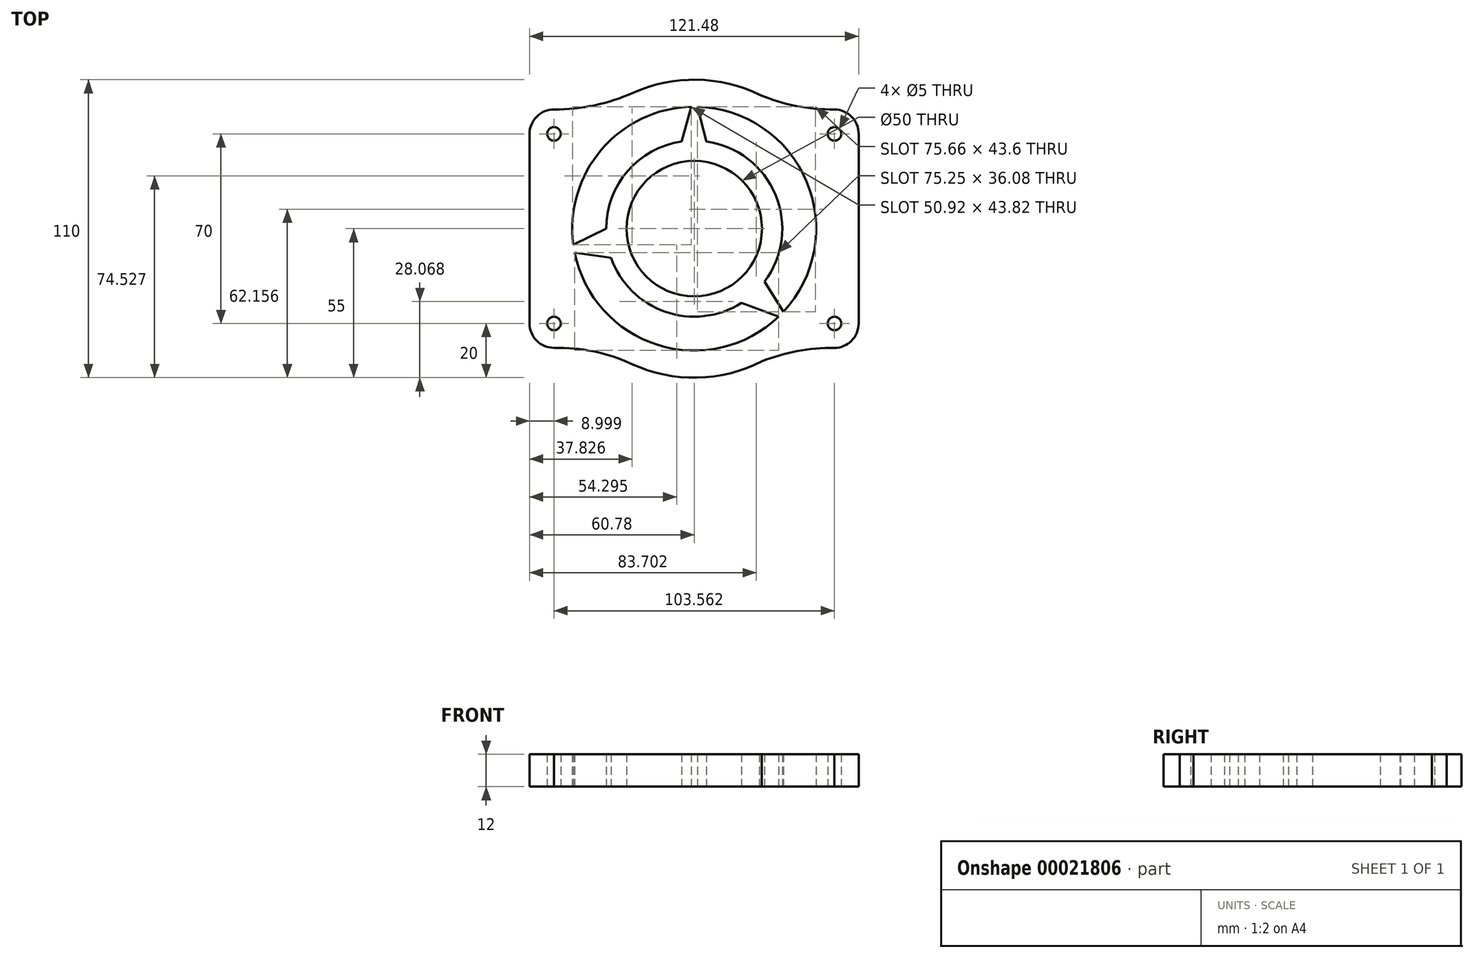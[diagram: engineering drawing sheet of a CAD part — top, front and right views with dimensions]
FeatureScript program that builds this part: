
annotation { "Feature Type Name" : "Feature", "Feature Type Description" : "" }
export const myFeature = defineFeature(function(context is Context, id is Id, definition is map)
    precondition{}
    {
        {
            var Q0;
            Q0=qCreatedBy(makeId("Top.planeOp"),FACE);
            var sketch = newSketch(context, id + "F0", { "sketchPlane" : qUnion([Q0])});
            skCircle(sketch, "E0", {"center": v(0, 0) * mm, "radius": 45 * mm});
            skArc(sketch, "E1", {"start": v(-23.02, -49.95) * mm, "mid": v(1.05, -54.99) * mm, "end": v(24.9, -49.04) * mm});
            skPoint(sketch, "E2", {"position": v(-51.78, 35) * mm});
            skPoint(sketch, "E3", {"position": v(-51.78, -35) * mm});
            skPoint(sketch, "E4.MirrorP", {"position": v(51.78, 35) * mm});
            skCircle(sketch, "E5", {"center": v(-51.78, 35) * mm, "radius": 2.5 * mm});
            skCircle(sketch, "E6", {"center": v(-51.78, -35) * mm, "radius": 2.5 * mm});
            skArc(sketch, "E7", {"start": v(-60.78, -35) * mm, "mid": v(-58.14, -41.36) * mm, "end": v(-51.78, -44) * mm});
            skArc(sketch, "E8", {"start": v(-51.78, 44) * mm, "mid": v(-58.14, 41.36) * mm, "end": v(-60.78, 35) * mm});
            skPoint(sketch, "E9", {"position": v(-60.78, 35) * mm});
            skPoint(sketch, "E10", {"position": v(-60.78, -35) * mm});
            skLineSegment(sketch, "E11", {"start": v(-60.78, 35) * mm, "end": v(-60.78, -35) * mm});
            skPoint(sketch, "E12.MirrorP", {"position": v(51.7, 35) * mm});
            skLineSegment(sketch, "E13.MirrorCS", {"start": v(60.7, 34.97) * mm, "end": v(60.7, -35.03) * mm});
            skPoint(sketch, "E14.MirrorP", {"position": v(51.7, -35.03) * mm});
            skArc(sketch, "E15.MirrorCS", {"start": v(51.78, 44) * mm, "mid": v(58.1, 41.33) * mm, "end": v(60.7, 34.97) * mm});
            skArc(sketch, "E16.MirrorCS", {"start": v(60.7, -35.03) * mm, "mid": v(58.07, -41.4) * mm, "end": v(51.7, -44.03) * mm});
            skPoint(sketch, "E17.MirrorP", {"position": v(60.7, 34.97) * mm});
            skPoint(sketch, "E18.MirrorP", {"position": v(60.7, -35.03) * mm});
            skArc(sketch, "E19.trimOffspring", {"start": v(24.1, 49.44) * mm, "mid": v(0.89, 55) * mm, "end": v(-22.5, 50.2) * mm});
            skPoint(sketch, "E20.MirrorP", {"position": v(-51.7, -35.03) * mm});
            skCircle(sketch, "E21.MirrorC", {"center": v(51.78, 35) * mm, "radius": 2.5 * mm});
            skCircle(sketch, "E22.MirrorC", {"center": v(51.78, -35) * mm, "radius": 2.5 * mm});
            skArc(sketch, "E23", {"start": v(-22.96, -49.98) * mm, "mid": v(-37.03, -45.35) * mm, "end": v(-51.78, -44) * mm});
            skArc(sketch, "E24", {"start": v(51.7, -44.03) * mm, "mid": v(38.05, -45.18) * mm, "end": v(24.9, -49.04) * mm});
            skArc(sketch, "E25", {"start": v(-51.78, 44) * mm, "mid": v(-36.81, 45.55) * mm, "end": v(-22.5, 50.2) * mm});
            skArc(sketch, "E26", {"start": v(24.1, 49.44) * mm, "mid": v(37.66, 45.3) * mm, "end": v(51.78, 44) * mm});
            skCircle(sketch, "E27", {"center": v(0, 0) * mm, "radius": 25 * mm});
            skCircle(sketch, "E28", {"center": v(0, 0) * mm, "radius": 32.5 * mm});
            skLineSegment(sketch, "E29", {"start": v(-1.04, 44.99) * mm, "end": v(-4.6, 32.17) * mm});
            skLineSegment(sketch, "E30", {"start": v(1.12, 44.99) * mm, "end": v(4.52, 32.18) * mm});
            skLineSegment(sketch, "E31", {"start": v(25.97, -19.54) * mm, "end": v(32.92, -30.68) * mm});
            skLineSegment(sketch, "E32", {"start": v(31.14, -32.48) * mm, "end": v(17.4, -27.45) * mm});
            skLineSegment(sketch, "E33", {"start": v(17.4, -27.45) * mm, "end": v(18.67, -26.5) * mm});
            skLineSegment(sketch, "E34", {"start": v(-30.66, -10.78) * mm, "end": v(-44.11, -8.9) * mm});
            skLineSegment(sketch, "E35", {"start": v(-44.6, -5.93) * mm, "end": v(-32.5, 0) * mm});
            skLineSegment(sketch, "E36", {"start": v(-32.5, 0) * mm, "end": v(-32.52, -1.33) * mm});
            skSolve(sketch);
        }
        {
            var Q0;
            Q0 = qSketchRegion(id + "F0", true);
            var Q1;
            {var subQ0=sQuery(id+"F0.wireOp",EDGE,"E29");Q1=makeQuery(id+"F0.imprint","IMPRINT",FACE,{"disambiguationData":[TD([[makeQuery(id+"F0.imprint","IMPRINT",EDGE,{"derivedFrom":subQ0}),1.0]])]});}
            var Q2;
            Q2=makeQuery(id+"F0.imprint","IMPRINT",FACE,{"disambiguationData":[TD([[makeQuery(id+"F0.imprint","IMPRINT",EDGE,{"derivedFrom":sQuery(id+"F0.wireOp",EDGE,"E27")}),-1.0]])]});
            var Q3;
            {var subQ0=sQuery(id+"F0.wireOp",EDGE,"E31");Q3=makeQuery(id+"F0.imprint","IMPRINT",FACE,{"disambiguationData":[TD([[makeQuery(id+"F0.imprint","IMPRINT",EDGE,{"derivedFrom":subQ0}),-1.0]])]});}
            var Q4;
            {var subQ0=sQuery(id+"F0.wireOp",EDGE,"E34");Q4=makeQuery(id+"F0.imprint","IMPRINT",FACE,{"disambiguationData":[TD([[makeQuery(id+"F0.imprint","IMPRINT",EDGE,{"derivedFrom":subQ0}),-1.0]])]});}
            extrude(context, id + "F1", {"entities" : qUnion([Q0, Q1, Q2, Q3, Q4]), "depth" : 12 * mm});
        }
    });
